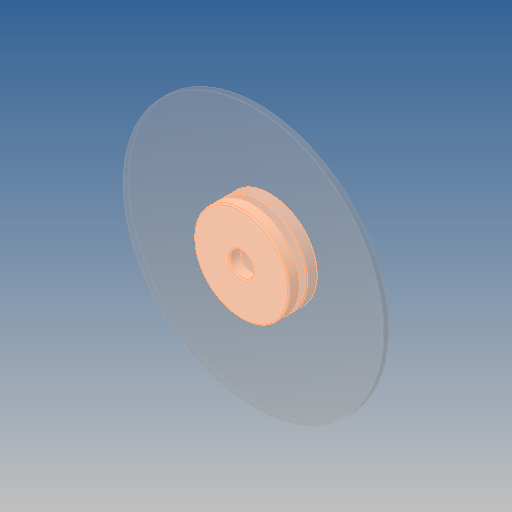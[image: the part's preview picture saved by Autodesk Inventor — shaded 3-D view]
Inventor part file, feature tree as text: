
AUTODESK INVENTOR PART (.ipt)
format: ipt  version: 2020 (Build 240168000, 168)  size: 180,224 bytes
history: mixed  units: mm
features: other x3, fillet x3, imported_body x1
ambient origin geometry x8: Origin, YZ Plane, XZ Plane, XY Plane, X Axis, Y Axis, Z Axis, Center Point
bodies: Body1 (imported_parasolid), Body2 (imported_parasolid), Body3 (imported_parasolid)
feature tree (7):
  other  "Твердое тело1"
  other  "Твердое тело2"
  other  "Твердое тело3"
  fillet  "Fillet1"  [1 undecoded]
  fillet  "Fillet2"  [1 undecoded]
  fillet  "Fillet3"  [1 undecoded]
  imported_body  NMx_Import_Brep_tag  [imported B-rep: ~21 faces, bbox_mm=[15.0, 0.0, 2.5]]
note: 3 required parameter values undecoded (feature->parameter linkage not recoverable at this tier; creation-order binding heuristic only, values carry confidence <= 0.55)
